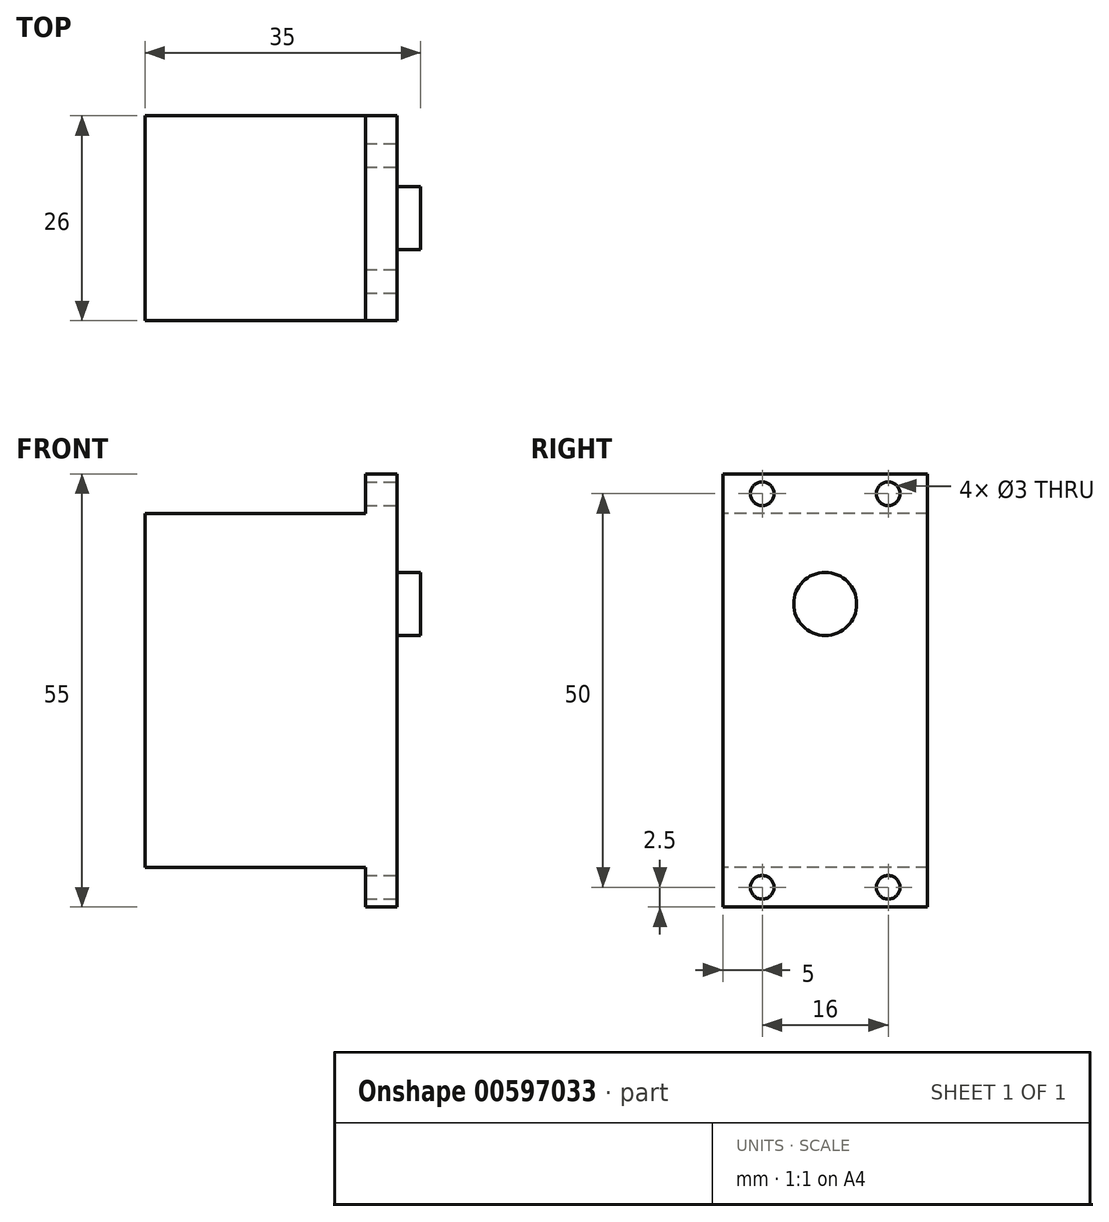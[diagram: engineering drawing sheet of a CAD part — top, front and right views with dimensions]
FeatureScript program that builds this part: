
annotation { "Feature Type Name" : "Feature", "Feature Type Description" : "" }
export const myFeature = defineFeature(function(context is Context, id is Id, definition is map)
    precondition{}
    {
        {
            var Q0;
            Q0=qCreatedBy(makeId("Right.planeOp"),FACE);
            var sketch = newSketch(context, id + "F0", { "sketchPlane" : qUnion([Q0])});
            skLineSegment(sketch, "E0.bottom", {"start": v(13, 25) * mm, "end": v(-13, 25) * mm});
            skLineSegment(sketch, "E0.top", {"start": v(13, -25) * mm, "end": v(-13, -25) * mm});
            skLineSegment(sketch, "E0.left", {"start": v(13, 25) * mm, "end": v(13, -25) * mm});
            skLineSegment(sketch, "E0.right", {"start": v(-13, 25) * mm, "end": v(-13, -25) * mm});
            skPoint(sketch, "E0.middle", {"position": v(0, 0) * mm});
            skSolve(sketch);
        }
        {
            var Q0;
            Q0=makeQuery(id+"F0.imprint","IMPRINT",FACE,{"disambiguationData":[TD([[makeQuery(id+"F0.imprint","IMPRINT",EDGE,{"derivedFrom":sQuery(id+"F0.wireOp",EDGE,"E0.bottom")}),1.0]])]});
            extrude(context, id + "F1", {"entities" : qUnion([Q0]), "endBound" : BoundingType.SYMMETRIC, "depth" : 32 * mm, "offsetDistance" : 25.4 * mm});
        }
        {
            var Q0;
            Q0=makeQuery(id+"F1.opExtrude","CAP_FACE",FACE,{"disambiguationData":[OSD([sQuery(id+"F0.wireOp",EDGE,"E0.bottom"),sQuery(id+"F0.wireOp",EDGE,"E0.top"),sQuery(id+"F0.wireOp",EDGE,"E0.left"),sQuery(id+"F0.wireOp",EDGE,"E0.right")])],"isStart":false});
            var sketch = newSketch(context, id + "F2", { "sketchPlane" : qUnion([Q0])});
            skCircle(sketch, "E1", {"center": v(0, 13.5) * mm, "radius": 4 * mm});
            skPoint(sketch, "E1.centerSnap0", {"position": v(0, 25) * mm});
            skSolve(sketch);
        }
        {
            var Q0;
            Q0=makeQuery(id+"F2.imprint","IMPRINT",FACE,{"disambiguationData":[TD([[makeQuery(id+"F2.imprint","IMPRINT",EDGE,{"derivedFrom":sQuery(id+"F2.wireOp",EDGE,"E1")}),1.0]])]});
            extrude(context, id + "F3", {"entities" : qUnion([Q0]), "operationType" : NewBodyOperationType.ADD, "depth" : 3 * mm, "offsetDistance" : 25.4 * mm});
        }
        {
            var Q0;
            Q0=makeQuery(id+"F1.opExtrude","SWEPT_FACE",FACE,{"disambiguationData":[OSD([sQuery(id+"F0.wireOp",EDGE,"E0.right")])]});
            var sketch = newSketch(context, id + "F4", { "sketchPlane" : qUnion([Q0])});
            skLineSegment(sketch, "E2.bottom", {"start": v(-16, -25) * mm, "end": v(12, -25) * mm});
            skLineSegment(sketch, "E2.top", {"start": v(-16, -20) * mm, "end": v(12, -20) * mm});
            skLineSegment(sketch, "E2.left", {"start": v(-16, -25) * mm, "end": v(-16, -20) * mm});
            skLineSegment(sketch, "E2.right", {"start": v(12, -25) * mm, "end": v(12, -20) * mm});
            skSolve(sketch);
        }
        {
            var Q0;
            Q0=makeQuery(id+"F4.imprint","IMPRINT",FACE,{"disambiguationData":[TD([[makeQuery(id+"F4.imprint","IMPRINT",EDGE,{"derivedFrom":sQuery(id+"F4.wireOp",EDGE,"E2.bottom")}),-1.0]])]});
            extrude(context, id + "F5", {"entities" : qUnion([Q0]), "operationType" : NewBodyOperationType.REMOVE, "oppositeDirection" : true, "depth" : 1320.8 * mm, "offsetDistance" : 25.4 * mm});
        }
        {
            var Q0;
            Q0=makeQuery(id+"F1.opExtrude","CAP_FACE",FACE,{"disambiguationData":[OSD([sQuery(id+"F0.wireOp",EDGE,"E0.bottom"),sQuery(id+"F0.wireOp",EDGE,"E0.top"),sQuery(id+"F0.wireOp",EDGE,"E0.left"),sQuery(id+"F0.wireOp",EDGE,"E0.right")])],"isStart":false});
            var sketch = newSketch(context, id + "F6", { "sketchPlane" : qUnion([Q0])});
            skLineSegment(sketch, "E3.bottom", {"start": v(-13, 25) * mm, "end": v(13, 25) * mm});
            skLineSegment(sketch, "E3.top", {"start": v(-13, 30) * mm, "end": v(13, 30) * mm});
            skLineSegment(sketch, "E3.left", {"start": v(-13, 25) * mm, "end": v(-13, 30) * mm});
            skLineSegment(sketch, "E3.right", {"start": v(13, 25) * mm, "end": v(13, 30) * mm});
            skCircle(sketch, "E4", {"center": v(-8, 27.5) * mm, "radius": 1.5 * mm});
            skCircle(sketch, "E5", {"center": v(8, 27.5) * mm, "radius": 1.5 * mm});
            skLineSegment(sketch, "E6", {"start": v(0, 30) * mm, "end": v(0, 25) * mm, "construction": true});
            skSolve(sketch);
        }
        {
            var Q0;
            Q0=makeQuery(id+"F6.imprint","IMPRINT",FACE,{"disambiguationData":[TD([[makeQuery(id+"F6.imprint","IMPRINT",EDGE,{"derivedFrom":sQuery(id+"F6.wireOp",EDGE,"E3.bottom")}),-1.0]])]});
            extrude(context, id + "F7", {"entities" : qUnion([Q0]), "operationType" : NewBodyOperationType.ADD, "oppositeDirection" : true, "depth" : 4 * mm, "offsetDistance" : 25.4 * mm});
        }
        {
            var Q0;
            Q0=makeQuery(id+"F7.boolean.opBoolean","MERGE",FACE,{"derivedFrom":[makeQuery(id+"F1.opExtrude","CAP_FACE",FACE,{"disambiguationData":[OSD([sQuery(id+"F0.wireOp",EDGE,"E0.bottom"),sQuery(id+"F0.wireOp",EDGE,"E0.top"),sQuery(id+"F0.wireOp",EDGE,"E0.left"),sQuery(id+"F0.wireOp",EDGE,"E0.right")])],"isStart":false}),makeQuery(id+"F7.opExtrude","CAP_FACE",FACE,{"disambiguationData":[OSD([sQuery(id+"F6.wireOp",EDGE,"E3.bottom"),sQuery(id+"F6.wireOp",EDGE,"E3.top"),sQuery(id+"F6.wireOp",EDGE,"E3.left"),sQuery(id+"F6.wireOp",EDGE,"E3.right"),sQuery(id+"F6.wireOp",EDGE,"E4"),sQuery(id+"F6.wireOp",EDGE,"E5")])],"isStart":true})]});
            var sketch = newSketch(context, id + "F8", { "sketchPlane" : qUnion([Q0])});
            skLineSegment(sketch, "E7", {"start": v(0, 30) * mm, "end": v(0, -25) * mm, "construction": true});
            skCircle(sketch, "E8", {"center": v(-8, -22.5) * mm, "radius": 1.5 * mm});
            skCircle(sketch, "E9", {"center": v(8, -22.5) * mm, "radius": 1.5 * mm});
            skSolve(sketch);
        }
        {
            var Q0;
            Q0=makeQuery(id+"F8.imprint","IMPRINT",FACE,{"disambiguationData":[TD([[makeQuery(id+"F8.imprint","IMPRINT",EDGE,{"derivedFrom":sQuery(id+"F8.wireOp",EDGE,"E8")}),1.0]])]});
            var Q1;
            Q1=makeQuery(id+"F8.imprint","IMPRINT",FACE,{"disambiguationData":[TD([[makeQuery(id+"F8.imprint","IMPRINT",EDGE,{"derivedFrom":sQuery(id+"F8.wireOp",EDGE,"E9")}),1.0]])]});
            extrude(context, id + "F9", {"entities" : qUnion([Q0, Q1]), "operationType" : NewBodyOperationType.REMOVE, "oppositeDirection" : true, "depth" : 4 * mm, "offsetDistance" : 25.4 * mm});
        }
    });
